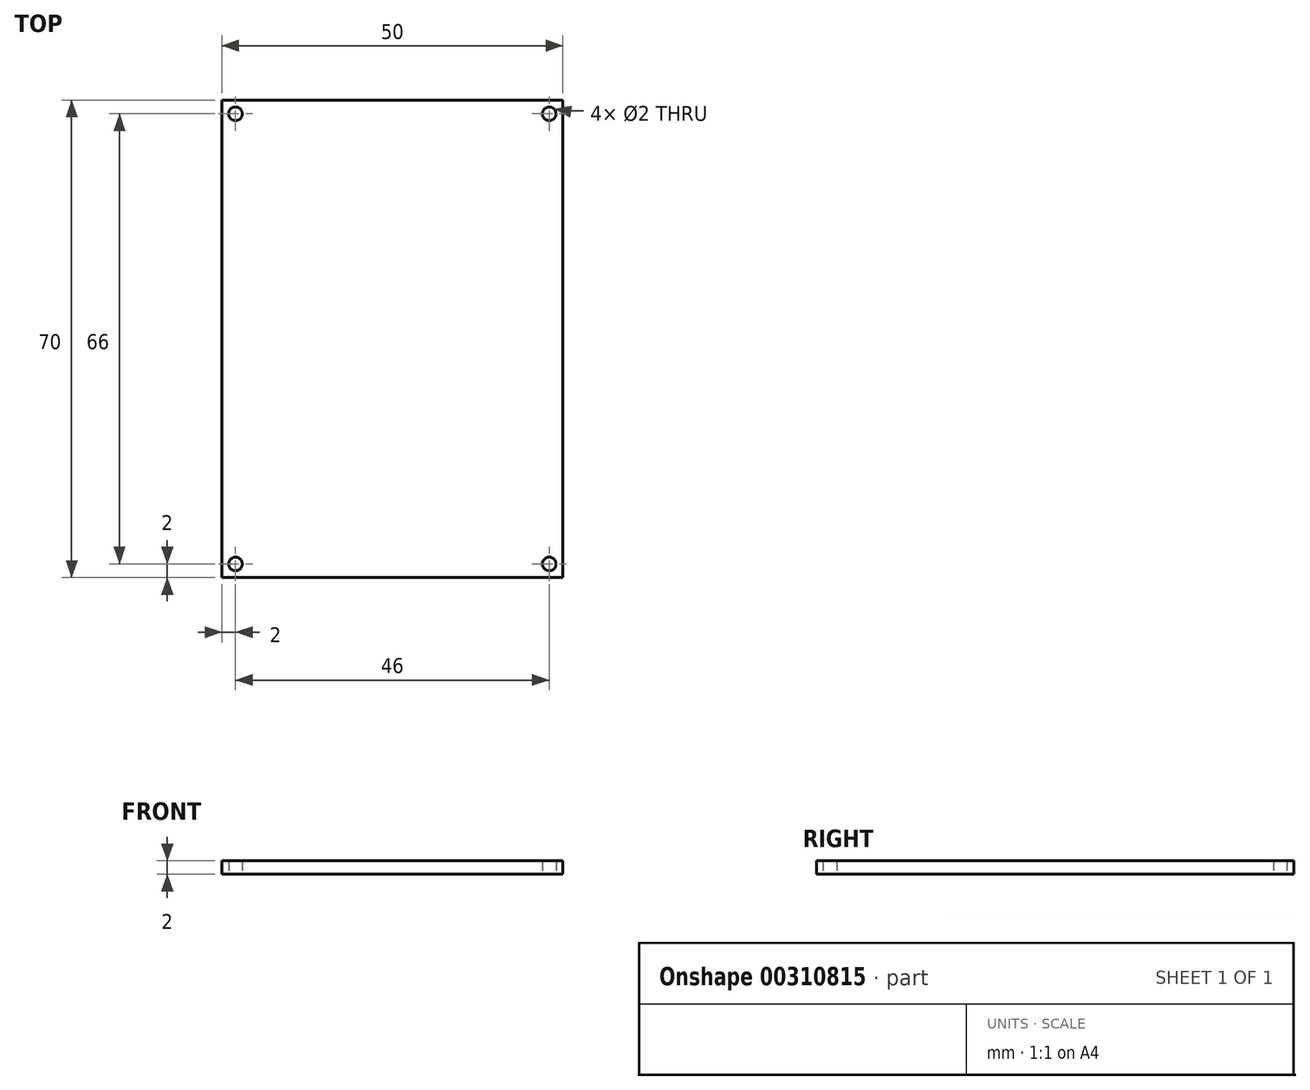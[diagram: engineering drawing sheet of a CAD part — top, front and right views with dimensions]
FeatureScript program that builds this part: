
annotation { "Feature Type Name" : "Feature", "Feature Type Description" : "" }
export const myFeature = defineFeature(function(context is Context, id is Id, definition is map)
    precondition{}
    {
        {
            var Q0;
            Q0=qCreatedBy(makeId("Top.planeOp"),FACE);
            var sketch = newSketch(context, id + "F0", { "sketchPlane" : qUnion([Q0])});
            skCircle(sketch, "E0", {"center": v(0, 0) * mm, "radius": 77.85 * mm});
            skSolve(sketch);
        }
        {
            var Q0;
            Q0=sQuery(id+"F0.wireOp",EDGE,"E0");
            extrude(context, id + "F1", {"bodyType" : ToolBodyType.SURFACE, "surfaceEntities" : qUnion([Q0]), "depth" : 187.74 * mm, "hasDraft" : true, "draftAngle" : 0.05 * radian});
        }
        {
            var Q0;
            Q0=makeQuery(id+"F1.opExtrude","SWEPT_BODY",BODY,{"disambiguationData":[OSD([sQuery(id+"F0.wireOp",EDGE,"E0")])]});
            deleteBodies(context, id + "F2", {"entities" : qUnion([Q0])});
        }
        {
            var Q0;
            Q0=qCreatedBy(makeId("Top.planeOp"),FACE);
            var sketch = newSketch(context, id + "F3", { "sketchPlane" : qUnion([Q0])});
            skLineSegment(sketch, "E1.bottom", {"start": v(-50, -70) * mm, "end": v(0, -70) * mm});
            skLineSegment(sketch, "E1.top", {"start": v(-50, 0) * mm, "end": v(0, 0) * mm});
            skLineSegment(sketch, "E1.left", {"start": v(-50, -70) * mm, "end": v(-50, 0) * mm});
            skLineSegment(sketch, "E1.right", {"start": v(0, -70) * mm, "end": v(0, 0) * mm});
            skCircle(sketch, "E2", {"center": v(-48, -2) * mm, "radius": 1 * mm});
            skLineSegment(sketch, "E3", {"start": v(-25, -70) * mm, "end": v(-25, 0) * mm, "construction": true});
            skLineSegment(sketch, "E4", {"start": v(-50, -35) * mm, "end": v(0, -35) * mm, "construction": true});
            skCircle(sketch, "E5.MirrorC", {"center": v(-2, -2) * mm, "radius": 1 * mm});
            skCircle(sketch, "E6.MirrorC", {"center": v(-48, -68) * mm, "radius": 1 * mm});
            skCircle(sketch, "E7.MirrorC", {"center": v(-2, -68) * mm, "radius": 1 * mm});
            skSolve(sketch);
        }
        {
            var Q0;
            Q0 = qSketchRegion(id + "F3", true);
            extrude(context, id + "F4", {"entities" : qUnion([Q0]), "depth" : 2 * mm});
        }
    });
